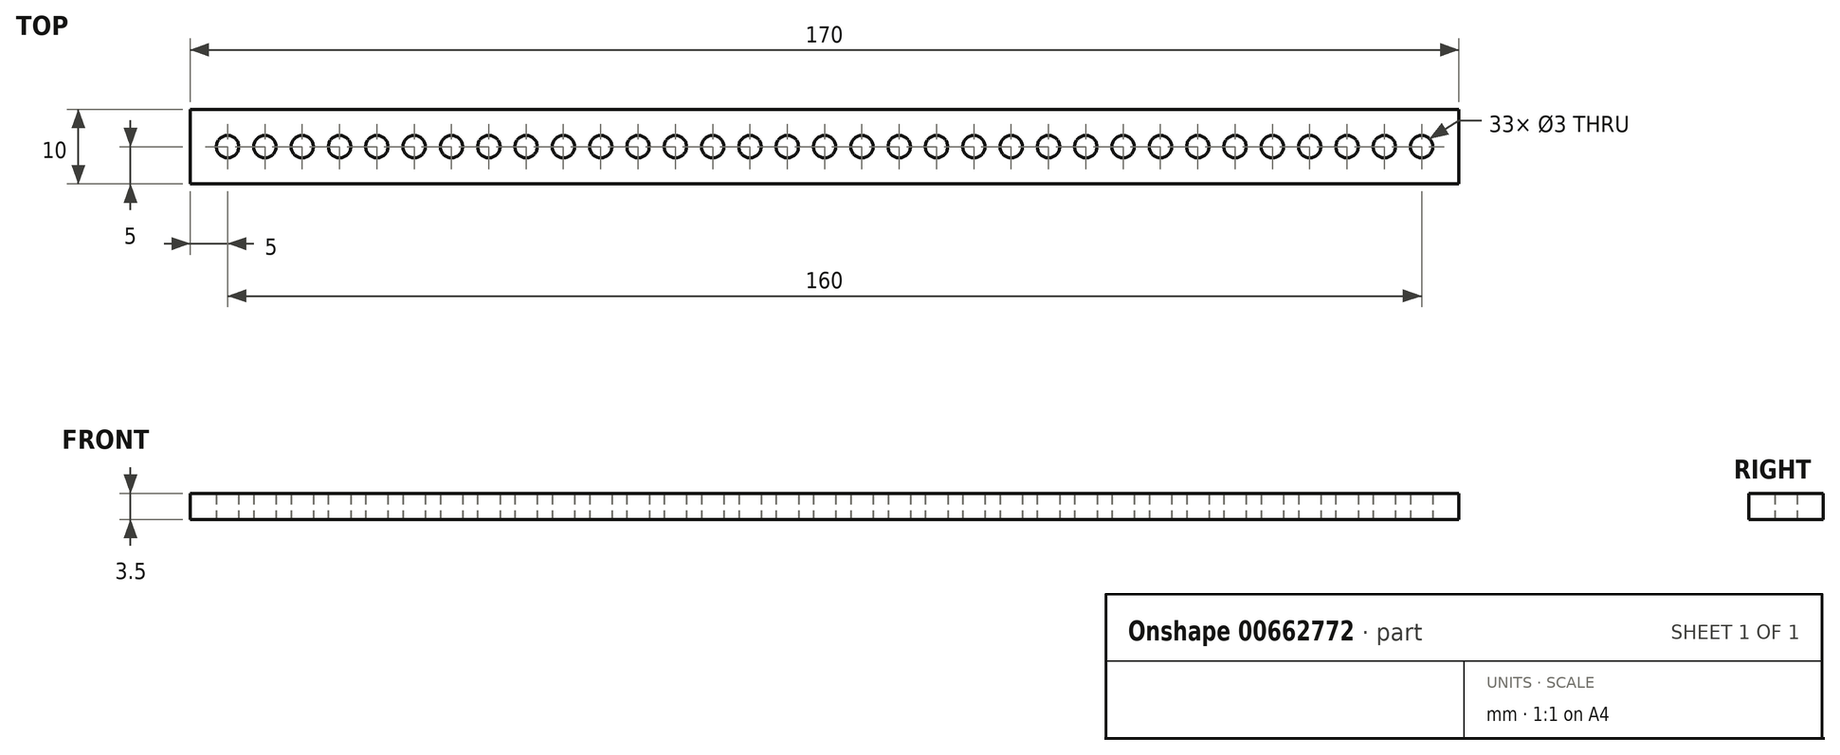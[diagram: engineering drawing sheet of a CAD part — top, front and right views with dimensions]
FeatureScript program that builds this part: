
annotation { "Feature Type Name" : "Feature", "Feature Type Description" : "" }
export const myFeature = defineFeature(function(context is Context, id is Id, definition is map)
    precondition{}
    {
        {
            var Q0;
            Q0=qCreatedBy(makeId("Top.planeOp"),FACE);
            var sketch = newSketch(context, id + "F0", { "sketchPlane" : qUnion([Q0])});
            skLineSegment(sketch, "E0.bottom", {"start": v(85, -5) * mm, "end": v(-85, -5) * mm});
            skLineSegment(sketch, "E0.top", {"start": v(85, 5) * mm, "end": v(-85, 5) * mm});
            skLineSegment(sketch, "E0.left", {"start": v(85, -5) * mm, "end": v(85, 5) * mm});
            skLineSegment(sketch, "E0.right", {"start": v(-85, -5) * mm, "end": v(-85, 5) * mm});
            skPoint(sketch, "E0.middle", {"position": v(0, 0) * mm});
            skLineSegment(sketch, "E1", {"start": v(-85, 0) * mm, "end": v(-80, 0) * mm, "construction": true});
            skCircle(sketch, "E2", {"center": v(-80, 0) * mm, "radius": 1.5 * mm});
            skCircle(sketch, "E3.1.0.0", {"center": v(-75, 0) * mm, "radius": 1.5 * mm});
            skCircle(sketch, "E3.2.0.0", {"center": v(-70, 0) * mm, "radius": 1.5 * mm});
            skCircle(sketch, "E3.3.0.0", {"center": v(-65, 0) * mm, "radius": 1.5 * mm});
            skCircle(sketch, "E3.4.0.0", {"center": v(-60, 0) * mm, "radius": 1.5 * mm});
            skCircle(sketch, "E3.5.0.0", {"center": v(-55, 0) * mm, "radius": 1.5 * mm});
            skCircle(sketch, "E3.6.0.0", {"center": v(-50, 0) * mm, "radius": 1.5 * mm});
            skCircle(sketch, "E3.7.0.0", {"center": v(-45, 0) * mm, "radius": 1.5 * mm});
            skCircle(sketch, "E3.8.0.0", {"center": v(-40, 0) * mm, "radius": 1.5 * mm});
            skCircle(sketch, "E3.9.0.0", {"center": v(-35, 0) * mm, "radius": 1.5 * mm});
            skCircle(sketch, "E3.10.0.0", {"center": v(-30, 0) * mm, "radius": 1.5 * mm});
            skCircle(sketch, "E3.11.0.0", {"center": v(-25, 0) * mm, "radius": 1.5 * mm});
            skCircle(sketch, "E3.12.0.0", {"center": v(-20, 0) * mm, "radius": 1.5 * mm});
            skCircle(sketch, "E3.13.0.0", {"center": v(-15, 0) * mm, "radius": 1.5 * mm});
            skCircle(sketch, "E3.14.0.0", {"center": v(-10, 0) * mm, "radius": 1.5 * mm});
            skCircle(sketch, "E3.15.0.0", {"center": v(-5, 0) * mm, "radius": 1.5 * mm});
            skCircle(sketch, "E3.16.0.0", {"center": v(0, 0) * mm, "radius": 1.5 * mm});
            skCircle(sketch, "E3.17.0.0", {"center": v(5, 0) * mm, "radius": 1.5 * mm});
            skCircle(sketch, "E3.18.0.0", {"center": v(10, 0) * mm, "radius": 1.5 * mm});
            skCircle(sketch, "E3.19.0.0", {"center": v(15, 0) * mm, "radius": 1.5 * mm});
            skCircle(sketch, "E3.20.0.0", {"center": v(20, 0) * mm, "radius": 1.5 * mm});
            skCircle(sketch, "E3.21.0.0", {"center": v(25, 0) * mm, "radius": 1.5 * mm});
            skCircle(sketch, "E3.22.0.0", {"center": v(30, 0) * mm, "radius": 1.5 * mm});
            skCircle(sketch, "E3.23.0.0", {"center": v(35, 0) * mm, "radius": 1.5 * mm});
            skCircle(sketch, "E3.24.0.0", {"center": v(40, 0) * mm, "radius": 1.5 * mm});
            skCircle(sketch, "E3.25.0.0", {"center": v(45, 0) * mm, "radius": 1.5 * mm});
            skCircle(sketch, "E3.26.0.0", {"center": v(50, 0) * mm, "radius": 1.5 * mm});
            skCircle(sketch, "E3.27.0.0", {"center": v(55, 0) * mm, "radius": 1.5 * mm});
            skCircle(sketch, "E3.28.0.0", {"center": v(60, 0) * mm, "radius": 1.5 * mm});
            skCircle(sketch, "E3.29.0.0", {"center": v(65, 0) * mm, "radius": 1.5 * mm});
            skCircle(sketch, "E3.30.0.0", {"center": v(70, 0) * mm, "radius": 1.5 * mm});
            skCircle(sketch, "E3.31.0.0", {"center": v(75, 0) * mm, "radius": 1.5 * mm});
            skCircle(sketch, "E3.32.0.0", {"center": v(80, 0) * mm, "radius": 1.5 * mm});
            skLineSegment(sketch, "E3.direction1", {"start": v(-80, 0) * mm, "end": v(-75, 0) * mm, "construction": true});
            skSolve(sketch);
        }
        {
            var Q0;
            Q0=makeQuery(id+"F0.imprint","IMPRINT",FACE,{"disambiguationData":[TD([[makeQuery(id+"F0.imprint","IMPRINT",EDGE,{"derivedFrom":sQuery(id+"F0.wireOp",EDGE,"E0.bottom")}),-1.0]])]});
            extrude(context, id + "F1", {"entities" : qUnion([Q0]), "depth" : 3.5 * mm, "offsetDistance" : 25 * mm});
        }
    });
